# Revit family: REVIT-DWST-2018
name_source: partatom
category: Mechanical Equipment
revit_build: Autodesk Revit 2018 (Build: 20190510_1515(x64)
units: mm (PartAtom-declared; Revit-internal decimal feet)

## family parameters
Always vertical = Yes
Cut with Voids When Loaded = No
Part Type = Normal
Room Calculation Point = No
Round Connector Dimension = Use Radius
Shared = No
Work Plane-Based = No

## types (8) — shared parameters
Assembly Code = D3040400
Controll Access Angle = 45.00°
Description = Storage Tanks for Hot Water
Disclaimer = This rendering is for building modeling purposes only. Submittal/catalog is still the contract document. PVI reserves the right to change design and specification without notice.
Drain Angle = 90.00°
Height to Upper Drain = 25 9/64"
Manufacturer = PVI Industries, LLC
Manway Access Radius = 6 1/2"
Relief NPT = 1"
Relief Radius = 1/2"
URL = www.pvi.com

## per-type parameters (varying)
- ADT-175-J: Cold Inlet Extension=19 1/2"; Cold Inlet Height=15 3/4"; Cold Inlet NPT=2"; Cold Inlet Radius=1"; Drain Extension=22 3/8"; Drain Height=3 1/2"; Drain NPT=1"; Drain Radius=1/2"; Flat Side Distance=34"; From Heater Extension=19 1/2"; From Heater Height=19"; From Heater NPT=2"; From Heater Radius=1"; Gallons Storage=175 CF; Hot Outlet NPT=2"; Hot Outlet Radius=1"; Manway Access Extension=1"; Model=L 175A-TR; Relief Angle=38.00°; Relief Extension=19 1/2"; Relief Height=59 5/16"; Skid Length=37"; Skid Spacing=17"; SkidWidthBetweenCenters=21"; To Heater Extension=19 1/2"; To Heater Height=27"; To Heater NPT=2"; To Heater Radius=1"; Unit Diameter=37"; Unit Height=71"; Unit Radius=18 1/2"; Weight=855
- ADT-215-J: Cold Inlet Extension=19 1/2"; Cold Inlet Height=15 3/4"; Cold Inlet NPT=2"; Cold Inlet Radius=1"; Drain Extension=22 3/8"; Drain Height=3 1/2"; Drain NPT=1"; Drain Radius=1/2"; Flat Side Distance=34"; From Heater Extension=19 1/2"; From Heater Height=19"; From Heater NPT=2"; From Heater Radius=1"; Gallons Storage=215 CF; Hot Outlet NPT=2"; Hot Outlet Radius=1"; Manway Access Extension=1"; Model=L 215A-TR; Relief Angle=38.00°; Relief Extension=19 1/2"; Relief Height=65 7/8"; Skid Length=37"; Skid Spacing=17"; SkidWidthBetweenCenters=21"; To Heater Extension=19 1/2"; To Heater Height=27"; To Heater NPT=2"; To Heater Radius=1"; Unit Diameter=37"; Unit Height=78"; Unit Radius=18 1/2"; Weight=895
- ADT-250-J: Cold Inlet Extension=24"; Cold Inlet Height=17 7/8"; Cold Inlet NPT=2"; Cold Inlet Radius=1"; Drain Extension=26 7/8"; Drain Height=3 1/2"; Drain NPT=1"; Drain Radius=1/2"; Flat Side Distance=45 255/256"; From Heater Extension=24"; From Heater Height=19"; From Heater NPT=2"; From Heater Radius=1"; Gallons Storage=250 CF; Hot Outlet NPT=2"; Hot Outlet Radius=1"; Manway Access Extension=26"; Model=L 250A-TR; Relief Angle=45.00°; Relief Extension=24"; Relief Height=46 1/4"; Skid Length=46"; Skid Spacing=27"; SkidWidthBetweenCenters=31"; To Heater Extension=24"; To Heater Height=27"; To Heater NPT=2"; To Heater Radius=1"; Unit Diameter=46"; Unit Height=63"; Unit Radius=23"; Weight=945
- ADT-300-J: Cold Inlet Extension=24"; Cold Inlet Height=17 7/8"; Cold Inlet NPT=2"; Cold Inlet Radius=1"; Drain Extension=26 7/8"; Drain Height=3 1/2"; Drain NPT=1"; Drain Radius=1/2"; Flat Side Distance=45 255/256"; From Heater Extension=24"; From Heater Height=19"; From Heater NPT=2"; From Heater Radius=1"; Gallons Storage=300 CF; Hot Outlet NPT=2"; Hot Outlet Radius=1"; Manway Access Extension=26"; Model=L 300A-TR; Relief Angle=45.00°; Relief Extension=24"; Relief Height=58 1/4"; Skid Length=46"; Skid Spacing=27"; SkidWidthBetweenCenters=31"; To Heater Extension=24"; To Heater Height=27"; To Heater NPT=2"; To Heater Radius=1"; Unit Diameter=46"; Unit Height=75"; Unit Radius=23"; Weight=1010
- ADT-400-J: Cold Inlet Extension=24"; Cold Inlet Height=17 7/8"; Cold Inlet NPT=2"; Cold Inlet Radius=1"; Drain Extension=26 7/8"; Drain Height=3 1/2"; Drain NPT=1"; Drain Radius=1/2"; Flat Side Distance=45 255/256"; From Heater Extension=24"; From Heater Height=19"; From Heater NPT=2"; From Heater Radius=1"; Gallons Storage=400 CF; Hot Outlet NPT=2"; Hot Outlet Radius=1"; Manway Access Extension=26"; Model=L 400A-TR; Relief Angle=45.00°; Relief Extension=24"; Relief Height=70 1/4"; Skid Length=46"; Skid Spacing=27"; SkidWidthBetweenCenters=31"; To Heater Extension=24"; To Heater Height=27"; To Heater NPT=2"; To Heater Radius=1"; Unit Diameter=46"; Unit Height=87"; Unit Radius=23"; Weight=1070
- ADT-500-J: Cold Inlet Extension=29"; Cold Inlet Height=19 3/4"; Cold Inlet NPT=3"; Cold Inlet Radius=1 1/2"; Drain Extension=31 7/8"; Drain Height=3 3/4"; Drain NPT=1 1/2"; Drain Radius=3/4"; Flat Side Distance=55 255/256"; From Heater Extension=29"; From Heater Height=24"; From Heater NPT=3"; From Heater Radius=1 1/2"; Gallons Storage=500 CF; Hot Outlet NPT=3"; Hot Outlet Radius=1 1/2"; Manway Access Extension=31"; Model=L 500A-TR; Relief Angle=38.00°; Relief Extension=29"; Relief Height=59 1/2"; Skid Length=54 1/2"; Skid Spacing=27"; SkidWidthBetweenCenters=31"; To Heater Extension=29"; To Heater Height=32"; To Heater NPT=3"; To Heater Radius=1 1/2"; Unit Diameter=56"; Unit Height=78"; Unit Radius=28"; Weight=1415
- ADT-600-J: Cold Inlet Extension=29"; Cold Inlet Height=19 3/4"; Cold Inlet NPT=3"; Cold Inlet Radius=1 1/2"; Drain Extension=31 7/8"; Drain Height=3 3/4"; Drain NPT=1 1/2"; Drain Radius=3/4"; Flat Side Distance=55 255/256"; From Heater Extension=29"; From Heater Height=24"; From Heater NPT=3"; From Heater Radius=1 1/2"; Gallons Storage=600 CF; Hot Outlet NPT=3"; Hot Outlet Radius=1 1/2"; Manway Access Extension=31"; Model=L 600A-TR; Relief Angle=38.00°; Relief Extension=29"; Relief Height=71 1/2"; Skid Length=54 1/2"; Skid Spacing=27"; SkidWidthBetweenCenters=31"; To Heater Extension=29"; To Heater Height=32"; To Heater NPT=3"; To Heater Radius=1 1/2"; Unit Diameter=56"; Unit Height=90"; Unit Radius=28"; Weight=1605
- ADT-750-J: Cold Inlet Extension=34 1/2"; Cold Inlet Height=22 1/2"; Cold Inlet NPT=3"; Cold Inlet Radius=1 1/2"; Drain Extension=37 3/8"; Drain Height=3 3/4"; Drain NPT=1 1/2"; Drain Radius=3/4"; Flat Side Distance=66 255/256"; From Heater Extension=34 1/2"; From Heater Height=24"; From Heater NPT=3"; From Heater Radius=1 1/2"; Gallons Storage=750 CF; Hot Outlet NPT=3"; Hot Outlet Radius=1 1/2"; Manway Access Extension=36 1/2"; Model=L 750A-TR; Relief Angle=45.00°; Relief Extension=34 1/2"; Relief Height=62 1/4"; Skid Length=68"; Skid Spacing=36"; SkidWidthBetweenCenters=40"; To Heater Extension=34 1/2"; To Heater Height=32"; To Heater NPT=3"; To Heater Radius=1 1/2"; Unit Diameter=67"; Unit Height=83"; Unit Radius=33 1/2"; Weight=1770

## geometry (parser evidence)
native form markers: Sweep x2
no freeform markers — native parametric forms only
